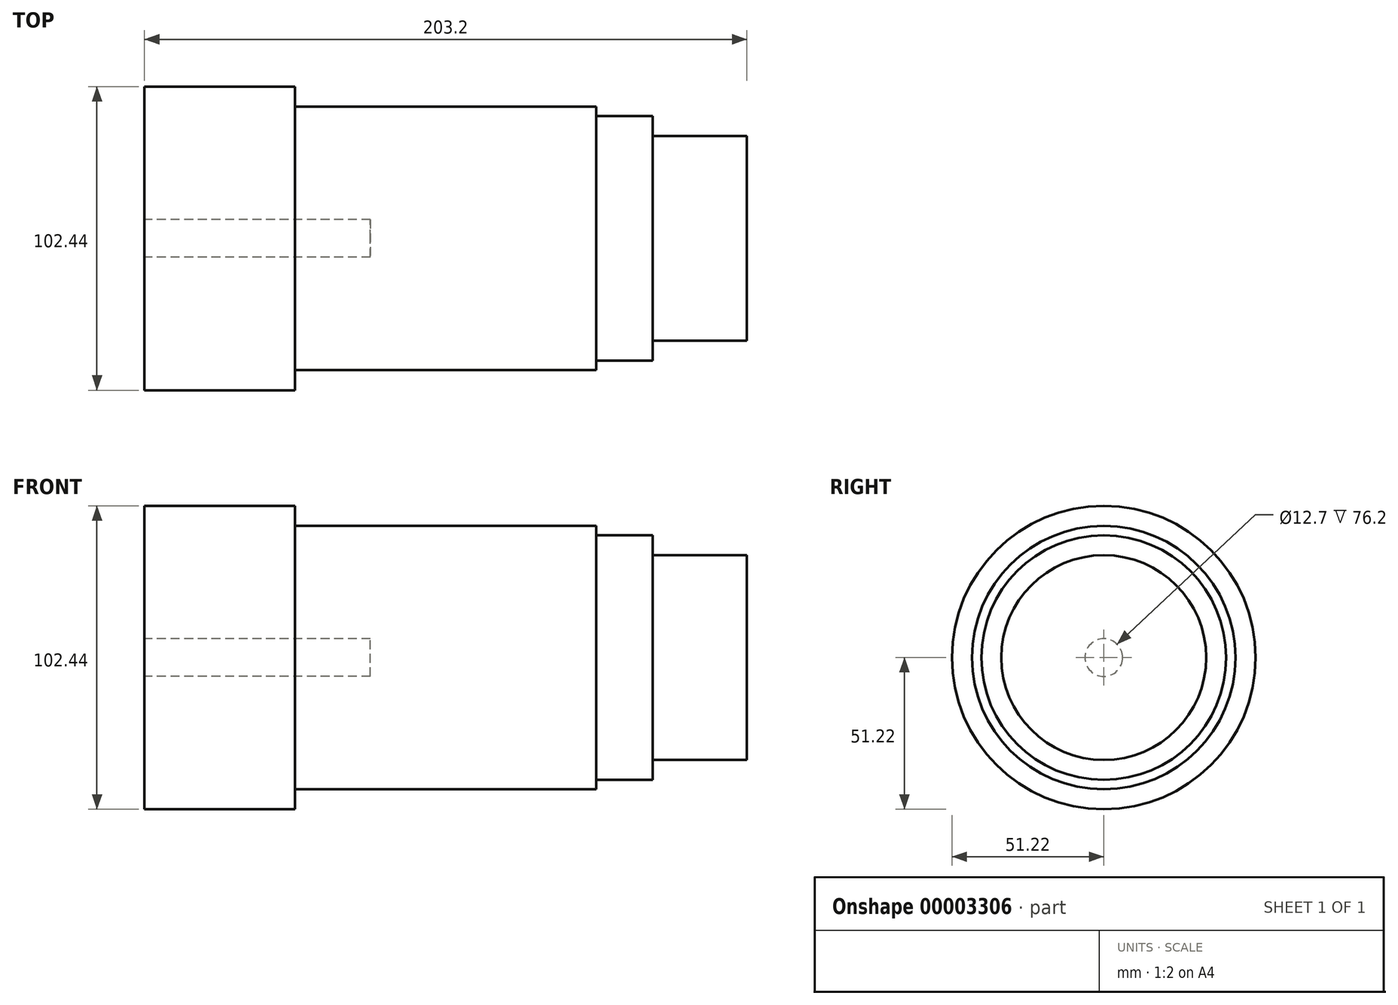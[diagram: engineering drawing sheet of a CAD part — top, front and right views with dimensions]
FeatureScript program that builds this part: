
annotation { "Feature Type Name" : "Feature", "Feature Type Description" : "" }
export const myFeature = defineFeature(function(context is Context, id is Id, definition is map)
    precondition{}
    {
        {
            var Q0;
            Q0=qCreatedBy(makeId("Front.planeOp"),FACE);
            var sketch = newSketch(context, id + "F0", { "sketchPlane" : qUnion([Q0])});
            skLineSegment(sketch, "E0.top", {"start": v(50.8, 44.45) * mm, "end": v(152.4, 44.45) * mm});
            skLineSegment(sketch, "E0.right", {"start": v(152.4, 41.28) * mm, "end": v(152.4, 44.45) * mm});
            skLineSegment(sketch, "E1.top", {"start": v(152.4, 41.28) * mm, "end": v(171.45, 41.28) * mm});
            skLineSegment(sketch, "E1.right", {"start": v(171.45, 34.54) * mm, "end": v(171.45, 41.28) * mm});
            skLineSegment(sketch, "E2.top", {"start": v(171.45, 34.54) * mm, "end": v(203.2, 34.54) * mm});
            skLineSegment(sketch, "E2.right", {"start": v(203.2, 0) * mm, "end": v(203.2, 34.54) * mm});
            skLineSegment(sketch, "E3", {"start": v(50.8, 0) * mm, "end": v(203.2, 0) * mm});
            skLineSegment(sketch, "E4", {"start": v(50.8, 44.45) * mm, "end": v(50.8, 0) * mm});
            skSolve(sketch);
        }
        {
            var Q0;
            Q0=qCreatedBy(makeId("Front.planeOp"),FACE);
            var sketch = newSketch(context, id + "F1", { "sketchPlane" : qUnion([Q0])});
            skLineSegment(sketch, "E5.bottom", {"start": v(0, 0) * mm, "end": v(50.8, 0) * mm});
            skLineSegment(sketch, "E5.top", {"start": v(0, 51.22) * mm, "end": v(50.8, 51.22) * mm});
            skLineSegment(sketch, "E5.left", {"start": v(0, 0) * mm, "end": v(0, 51.22) * mm});
            skLineSegment(sketch, "E5.right", {"start": v(50.8, 0) * mm, "end": v(50.8, 51.22) * mm});
            skSolve(sketch);
        }
        {
            var Q0;
            Q0 = qSketchRegion(id + "F0", true);
            var Q1;
            Q1=sQuery(id+"F0.wireOp",EDGE,"E3");
            revolve(context, id + "F2", {"entities" : qUnion([Q0]), "axis" : qUnion([Q1]), "revolveType" : RevolveType.FULL});
        }
        {
            var Q0;
            Q0=makeQuery(id+"F1.imprint","IMPRINT",FACE,{"disambiguationData":[TD([[makeQuery(id+"F1.imprint","IMPRINT",EDGE,{"derivedFrom":sQuery(id+"F1.wireOp",EDGE,"E5.bottom")}),1.0]])]});
            var Q1;
            Q1=sQuery(id+"F1.wireOp",EDGE,"E5.bottom");
            revolve(context, id + "F3", {"operationType" : NewBodyOperationType.ADD, "entities" : qUnion([Q0]), "axis" : qUnion([Q1]), "revolveType" : RevolveType.FULL});
        }
        {
            var Q0;
            Q0=qCreatedBy(makeId("Right.planeOp"),FACE);
            var sketch = newSketch(context, id + "F4", { "sketchPlane" : qUnion([Q0])});
            skCircle(sketch, "E6", {"center": v(0, 0) * mm, "radius": 6.35 * mm});
            skSolve(sketch);
        }
        {
            var Q0;
            Q0=makeQuery(id+"F4.imprint","IMPRINT",FACE,{"disambiguationData":[TD([[makeQuery(id+"F4.imprint","IMPRINT",EDGE,{"derivedFrom":sQuery(id+"F4.wireOp",EDGE,"E6")}),1.0]])]});
            extrude(context, id + "F5", {"entities" : qUnion([Q0]), "operationType" : NewBodyOperationType.REMOVE, "depth" : 76.2 * mm});
        }
    });
